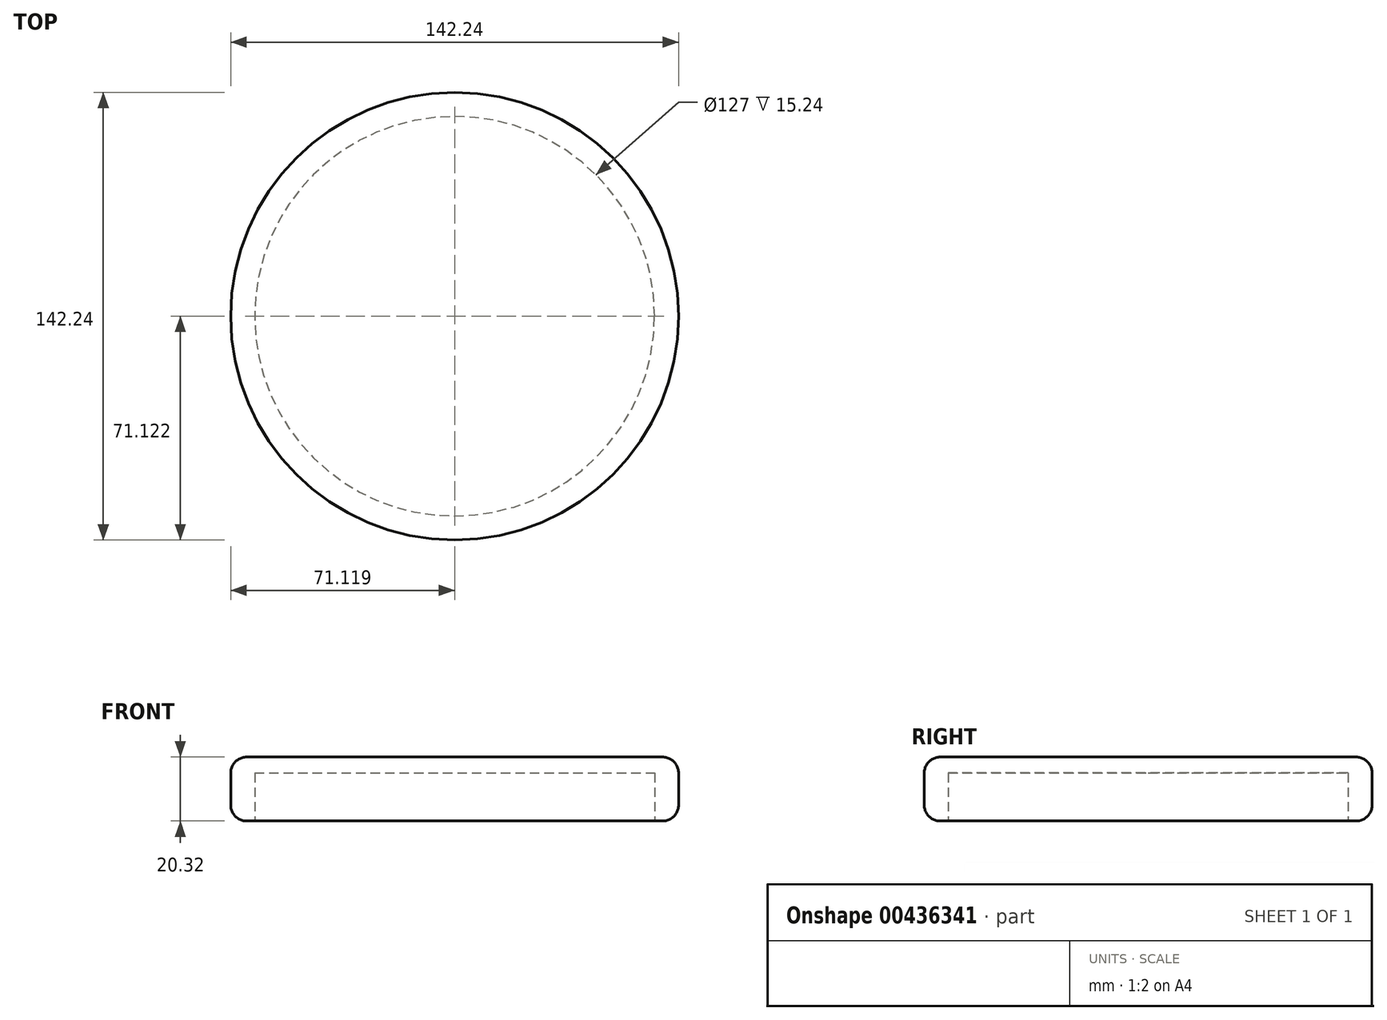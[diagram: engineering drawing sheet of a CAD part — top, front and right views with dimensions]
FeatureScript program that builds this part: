
annotation { "Feature Type Name" : "Feature", "Feature Type Description" : "" }
export const myFeature = defineFeature(function(context is Context, id is Id, definition is map)
    precondition{}
    {
        {
            var Q0;
            Q0=qCreatedBy(makeId("Top.planeOp"),FACE);
            var sketch = newSketch(context, id + "F0", { "sketchPlane" : qUnion([Q0])});
            skCircle(sketch, "E0", {"center": v(-28.4, 29.31) * mm, "radius": 71.12 * mm});
            skSolve(sketch);
        }
        {
            var Q0;
            Q0=makeQuery(id+"F0.imprint","IMPRINT",FACE,{"disambiguationData":[TD([[makeQuery(id+"F0.imprint","IMPRINT",EDGE,{"derivedFrom":sQuery(id+"F0.wireOp",EDGE,"E0")}),1.0]])]});
            var Q1;
            Q1=sQuery(id+"F0.wireOp",EDGE,"E0");
            extrude(context, id + "F1", {"entities" : qUnion([Q0]), "surfaceEntities" : qUnion([Q1]), "depth" : 20.32 * mm});
        }
        {
            var Q0;
            Q0=makeQuery(id+"F1.opExtrude","CAP_FACE",FACE,{"disambiguationData":[OSD([sQuery(id+"F0.wireOp",EDGE,"E0")])],"isStart":true});
            var sketch = newSketch(context, id + "F2", { "sketchPlane" : qUnion([Q0])});
            skCircle(sketch, "E1", {"center": v(-28.4, -29.31) * mm, "radius": 63.5 * mm});
            skSolve(sketch);
        }
        {
            var Q0;
            Q0=makeQuery(id+"F2.imprint","IMPRINT",FACE,{"disambiguationData":[TD([[makeQuery(id+"F2.imprint","IMPRINT",EDGE,{"derivedFrom":sQuery(id+"F2.wireOp",EDGE,"E1")}),1.0]])]});
            var Q1;
            Q1=sQuery(id+"F2.wireOp",EDGE,"E1");
            extrude(context, id + "F3", {"entities" : qUnion([Q0]), "operationType" : NewBodyOperationType.REMOVE, "surfaceEntities" : qUnion([Q1]), "oppositeDirection" : true, "depth" : 15.24 * mm});
        }
        {
            var Q0;
            Q0=makeQuery(id+"F1.opExtrude","CAP_EDGE",EDGE,{"disambiguationData":[OSD([sQuery(id+"F0.wireOp",EDGE,"E0")])],"isStart":false});
            var Q1;
            Q1=makeQuery(id+"F1.opExtrude","CAP_EDGE",EDGE,{"disambiguationData":[OSD([sQuery(id+"F0.wireOp",EDGE,"E0")])],"isStart":true});
            fillet(context, id + "F4", {"entities" : qUnion([Q0, Q1]), "radius" : 5.08 * mm, "tangentPropagation" : true, "allowEdgeOverflow" : false});
        }
    });
